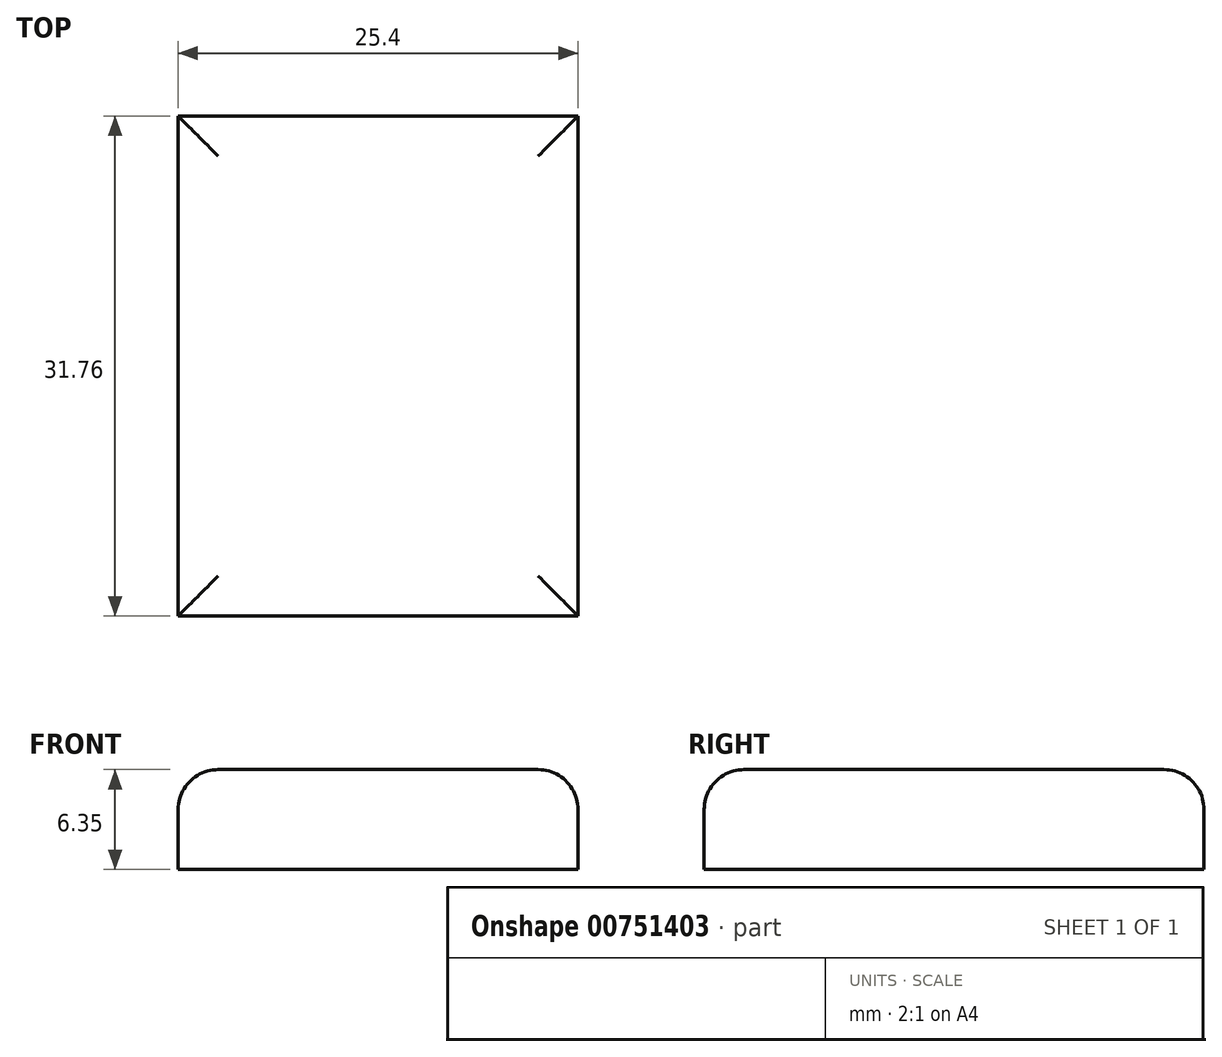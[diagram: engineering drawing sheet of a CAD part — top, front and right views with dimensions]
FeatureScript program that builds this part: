
annotation { "Feature Type Name" : "Feature", "Feature Type Description" : "" }
export const myFeature = defineFeature(function(context is Context, id is Id, definition is map)
    precondition{}
    {
        {
            var Q0;
            Q0=qCreatedBy(makeId("Top.planeOp"),FACE);
            var sketch = newSketch(context, id + "F0", { "sketchPlane" : qUnion([Q0])});
            skLineSegment(sketch, "E0.bottom", {"start": v(-12.7, 15.87) * mm, "end": v(12.7, 15.87) * mm});
            skLineSegment(sketch, "E0.top", {"start": v(-12.7, -15.88) * mm, "end": v(12.7, -15.88) * mm});
            skLineSegment(sketch, "E0.left", {"start": v(-12.7, 15.87) * mm, "end": v(-12.7, -15.88) * mm});
            skLineSegment(sketch, "E0.right", {"start": v(12.7, 15.87) * mm, "end": v(12.7, -15.88) * mm});
            skLineSegment(sketch, "E1", {"start": v(12.7, 15.88) * mm, "end": v(-12.7, -15.88) * mm, "construction": true});
            skLineSegment(sketch, "E2", {"start": v(12.7, -15.88) * mm, "end": v(-12.7, 15.88) * mm, "construction": true});
            skPoint(sketch, "E3", {"position": v(0, 0) * mm});
            skSolve(sketch);
        }
        {
            var Q0;
            Q0=makeQuery(id+"F0.imprint","IMPRINT",FACE,{"disambiguationData":[TD([[makeQuery(id+"F0.imprint","IMPRINT",EDGE,{"derivedFrom":sQuery(id+"F0.wireOp",EDGE,"E0.bottom")}),-1.0]])]});
            extrude(context, id + "F1", {"entities" : qUnion([Q0]), "depth" : 6.35 * mm, "offsetDistance" : 25.4 * mm});
        }
        {
            var Q0;
            Q0=makeQuery(id+"F1.opExtrude","CAP_EDGE",EDGE,{"disambiguationData":[OSD([sQuery(id+"F0.wireOp",EDGE,"E0.left")])],"isStart":false});
            var Q1;
            Q1=makeQuery(id+"F1.opExtrude","CAP_EDGE",EDGE,{"disambiguationData":[OSD([sQuery(id+"F0.wireOp",EDGE,"E0.top")])],"isStart":false});
            var Q2;
            Q2=makeQuery(id+"F1.opExtrude","CAP_EDGE",EDGE,{"disambiguationData":[OSD([sQuery(id+"F0.wireOp",EDGE,"E0.right")])],"isStart":false});
            var Q3;
            Q3=makeQuery(id+"F1.opExtrude","CAP_EDGE",EDGE,{"disambiguationData":[OSD([sQuery(id+"F0.wireOp",EDGE,"E0.bottom")])],"isStart":false});
            fillet(context, id + "F2", {"entities" : qUnion([Q0, Q1, Q2, Q3]), "radius" : 2.54 * mm, "tangentPropagation" : true, "allowEdgeOverflow" : false});
        }
    });
